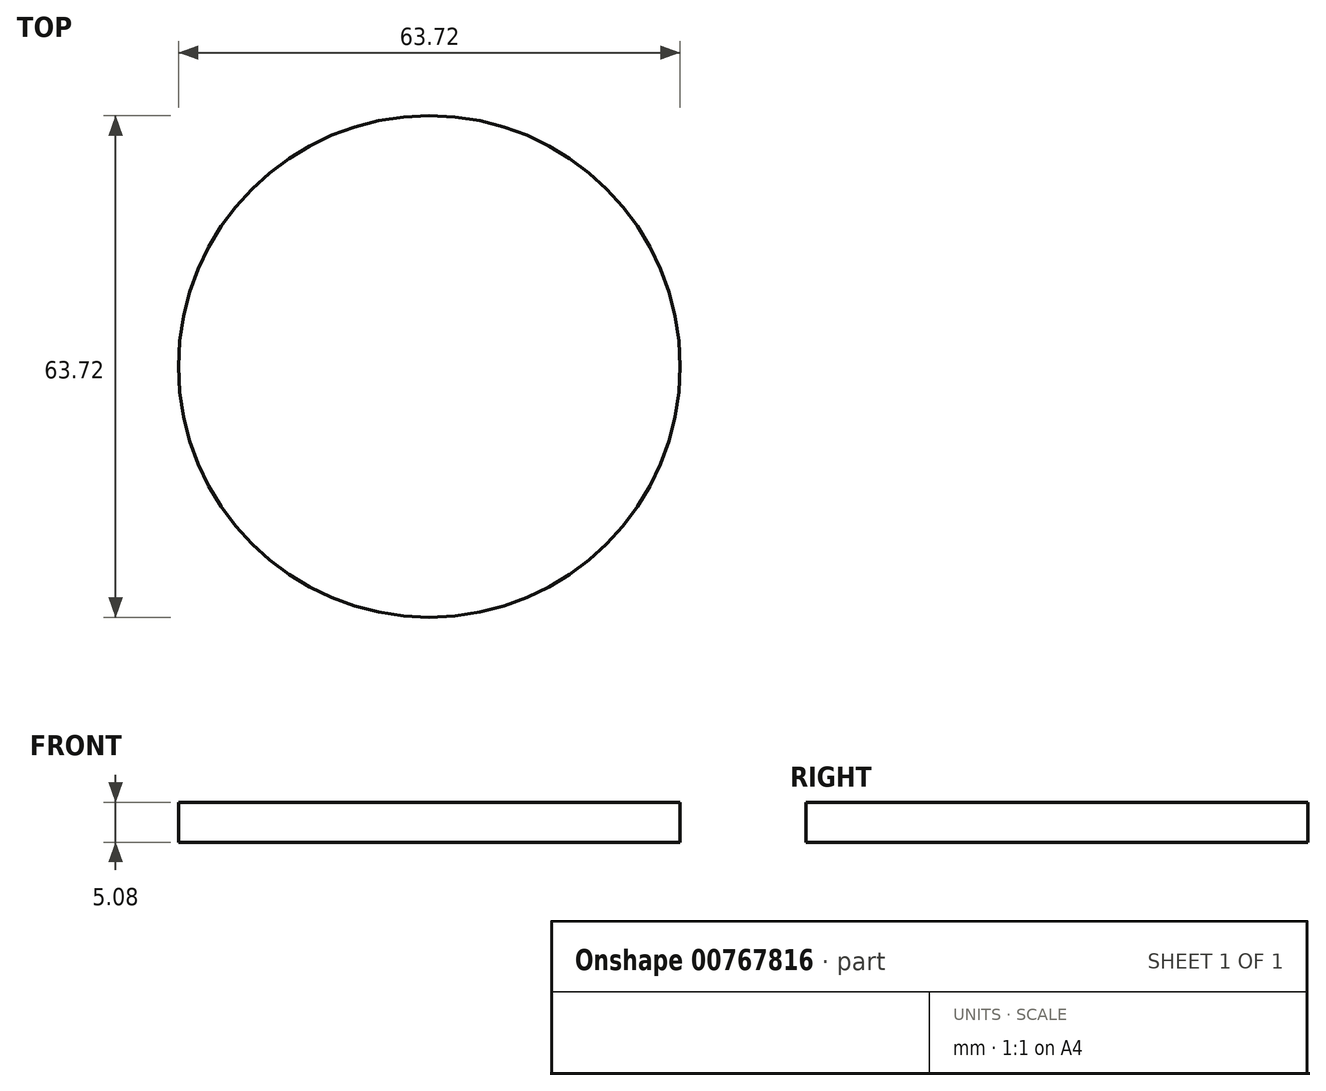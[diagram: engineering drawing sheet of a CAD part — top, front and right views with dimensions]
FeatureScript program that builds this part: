
annotation { "Feature Type Name" : "Feature", "Feature Type Description" : "" }
export const myFeature = defineFeature(function(context is Context, id is Id, definition is map)
    precondition{}
    {
        {
            var Q0;
            Q0=qCreatedBy(makeId("Top.planeOp"),FACE);
            var sketch = newSketch(context, id + "F0", { "sketchPlane" : qUnion([Q0])});
            skCircle(sketch, "E0", {"center": v(0, 0) * mm, "radius": 31.86 * mm});
            skSolve(sketch);
        }
        {
            var Q0;
            Q0=makeQuery(id+"F0.imprint","IMPRINT",FACE,{"disambiguationData":[TD([[makeQuery(id+"F0.imprint","IMPRINT",EDGE,{"derivedFrom":sQuery(id+"F0.wireOp",EDGE,"E0")}),1.0]])]});
            extrude(context, id + "F1", {"entities" : qUnion([Q0]), "depth" : 5.08 * mm, "offsetDistance" : 25.4 * mm});
        }
    });
